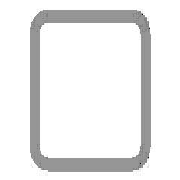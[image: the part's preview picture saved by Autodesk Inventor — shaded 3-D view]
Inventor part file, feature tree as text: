
AUTODESK INVENTOR PART (.ipt)
format: ipt  version: 2024 (Build 280153000, 153)  size: 129,024 bytes
history: native  units: mm (DEFAULTED — no unit token found)
features: other x4, extrude x1, sketch x1, plane x1
ambient origin geometry x8: Origin, YZ Plane, XZ Plane, XY Plane, X Axis, Y Axis, Z Axis, Center Point
bodies: Solid1 (feature_tree)
feature tree (7):
  parser-record x1  (decoder bookkeeping rows leaked as tree rows — omitted from the tree; the rows remain in map.json)
  other  "Driven Length"
  other  "Plano inicial"
  other  "Plano final"
  extrude  "Cuerpo"  TaperAngle=0.0deg  [1 undecoded]
  sketch  "Sketch3"  dims[d3=2890.0mm d4=0.0mm d10=50.8mm d11=50.8mm d12=3.175mm d13=-0.0mm d14=2890.0mm d15=25.4mm d16=25.4mm d17=6.35mm d18=90.0deg d19=2890.0mm]
  plane  "Work Plane3"
note: 1 required parameter value undecoded (feature->parameter linkage not recoverable at this tier; creation-order binding heuristic only, values carry confidence <= 0.55)
